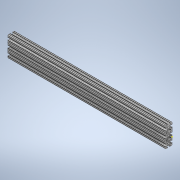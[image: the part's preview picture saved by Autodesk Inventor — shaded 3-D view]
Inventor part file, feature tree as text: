
AUTODESK INVENTOR PART (.ipt)
format: ipt  version: 2020 (Build 240168000, 168)  size: 379,904 bytes
history: native  units: in
note: dims shown in document units (in); Inventor stores cm internally (conversion verified against a paired STEP export)
features: sketch x2, extrude x1
ambient origin geometry x8: Origin, YZ Plane, XZ Plane, XY Plane, X Axis, Y Axis, Z Axis, Center Point
bodies: Solid1 (feature_tree)
feature tree (3):
  extrude  "Extrusion1"  [1 undecoded]
  sketch  "Sketch2"
  sketch  "Sketch1"  dims[d0=23.0in d1=0.0in]
note: 1 required parameter value undecoded (feature->parameter linkage not recoverable at this tier; creation-order binding heuristic only, values carry confidence <= 0.55)
